# Revit family: Козырёк YPS type 2.2.1 (С закладными кронштейнами) ДОРАБОТАТЬ
name_source: partatom
category: Обобщенные модели
units: mm (PartAtom-declared; Revit-internal decimal feet)

## family parameters
Всегда вертикально = Да
Может служить основой для арматурных стержней = Нет
На основе рабочей плоскости = Да
Общий = Да
При загрузке вырезать с полостями = Да
Размер круглого соединителя = Использовать диаметр
Сохранять ориентацию аннотаций = Нет
Тип детали = Нормальный
Точка принадлежности помещению = Нет

## types (3) — shared parameters
ADSK_Материал = Сталь, нержавеющая, полированная
G = 150 мм
const = 1 мм
Крепление в стену = 100 мм
zero-valued in all types: Отметка по умолчанию

## per-type parameters (varying)
| type | ADSK_Размер_Толщина | const Bkr | const H | Наименование стекла | Тип стеклодержателя |
| Козырёк YPS 2.2.1 (PSS) 8Зак.2EVA.8Зак | 16.8 мм | 74.26 мм | 146.631 мм | 8Зак.2EVA.8Зак | TF11X |
| Козырёк YPS 2.2.1 (PSS) 10Зак.2EVA.10Зак | 20.8 мм | 74.61 мм | 150.655 мм | 10Зак.2EVA.10Зак | TF17 |
| Козырёк YPS 2.2.1 (PSS) 6Зак.2EVA.6Зак | 12.8 мм | 73.91 мм | 142.615 мм | 6Зак.2EVA.6Зак | TF11X |

note: column(s) folded — value = type name in every type: ADSK_Наименование
